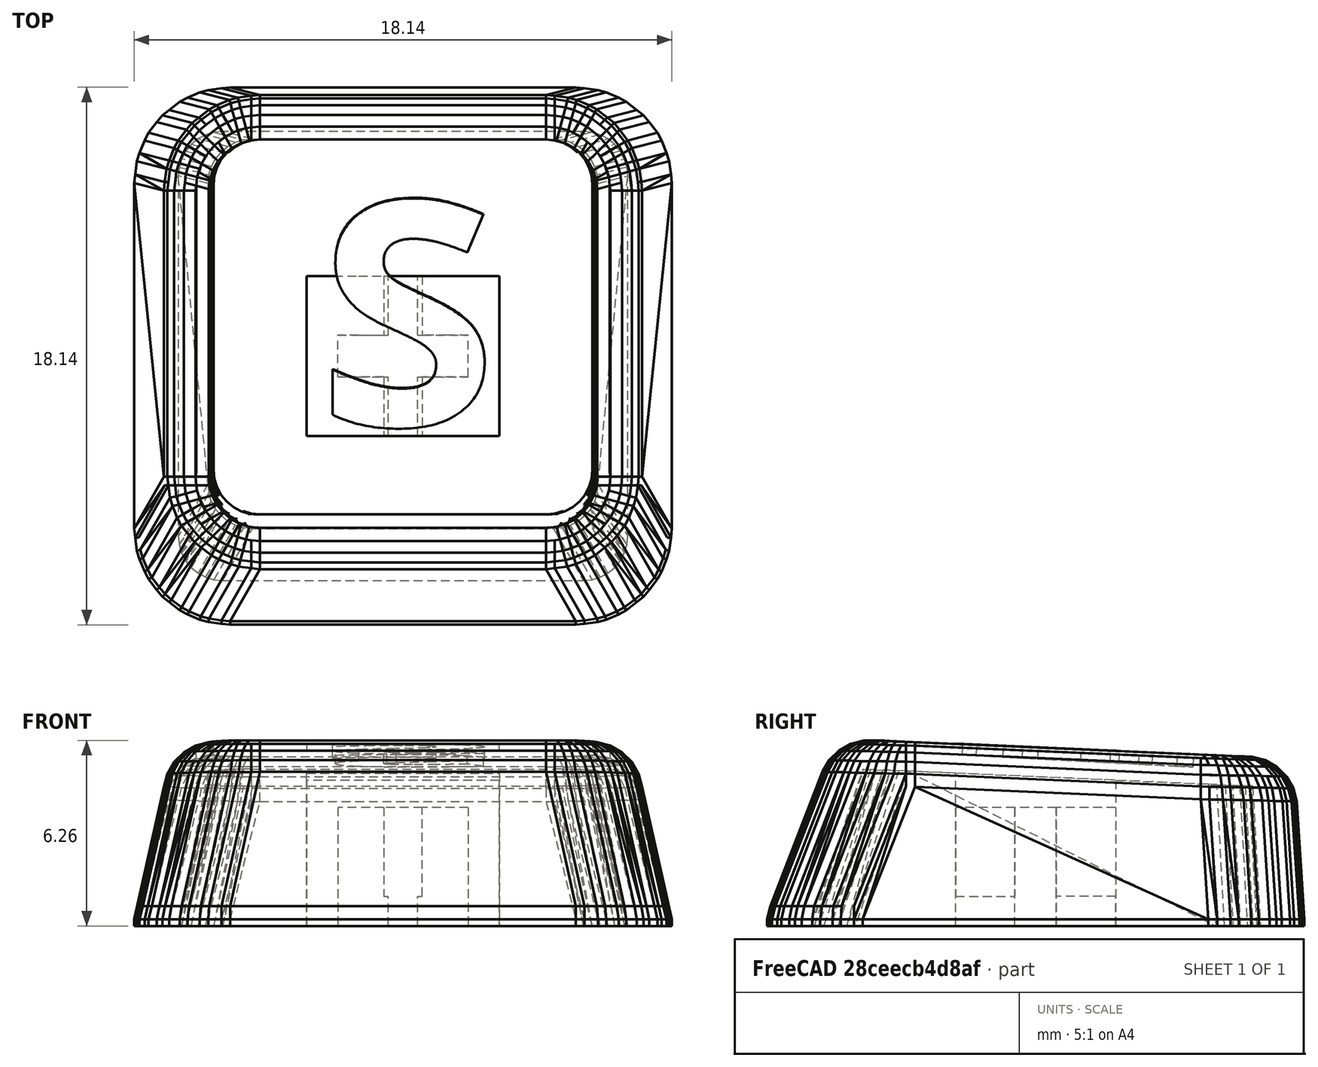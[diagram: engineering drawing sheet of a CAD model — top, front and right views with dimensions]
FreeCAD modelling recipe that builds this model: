
FCSTD DOCUMENT  (FreeCAD 0.18R16131 (Git))
Label: input
License: All rights reserved
LicenseURL: http://en.wikipedia.org/wiki/All_rights_reserved
objects: Part::Box×4, Part::Feature×1, Part::MultiFuse×1, Part::Part2DObjectPython×1, Part::Extrusion×1, Part::Cut×1
note: 9 computed .brp shape members not serialized (recipe doc carries the construction recipe); baked Part::Feature solids carry a one-line shape summary decoded from their .brp

FEATURE [Part::Feature] Solid
  shape: bbox 18.13 x 18.13 x 6.262 mm, 1259 faces (baked)
FEATURE [Part::Box] Box  label="Cube"
  AttacherType = Attacher::AttachEngine3D
  Height = 1
  Length = 1
  Placement = pos=(0.5,-2.7,0) rot=(0,0,1;0rad)
  Width = 2
FEATURE [Part::Box] Box001  label="Cube001"
  AttacherType = Attacher::AttachEngine3D
  Height = 1
  Length = 1
  Placement = pos=(-1.5,0.7,0) rot=(0,0,1;0rad)
  Width = 2
FEATURE [Part::Box] Box002  label="Cube002"
  AttacherType = Attacher::AttachEngine3D
  Height = 1
  Length = 1
  Placement = pos=(-1.5,-2.7,0) rot=(0,0,1;0rad)
  Width = 2
FEATURE [Part::Box] Box003  label="Cube003"
  AttacherType = Attacher::AttachEngine3D
  Height = 1
  Length = 1
  Placement = pos=(0.5,0.7,0) rot=(0,0,1;0rad)
  Width = 2
FEATURE [Part::MultiFuse] Fusion
  Shapes = -> [Solid,Box002,Box001,Box,Box003]
FEATURE [Part::Part2DObjectPython] ShapeString  # Draft 2D object (typed FeaturePython)
  FontFile = <userpath>/A6E4-ED97/3dprinting/fonts/open-sans/OpenSans-Bold.ttf
  Placement = pos=(-36.88,31.64,36.88) rot=(0,1,0;0rad)
  Size = 10
  String = S
  Tracking = 0
FEATURE [Part::Extrusion] Extrude
  Base = -> ShapeString
  Dir = (0,0,1)
  DirMode = 2
  FaceMakerClass = Part::FaceMakerBullseye
  LengthFwd = 0.5
  LengthRev = 0
  Placement = pos=(34,-36,-29.4) rot=(1,0,0;-0.05236rad)
  Solid = false
  Symmetric = false
FEATURE [Part::Cut] Cut
  Base = -> Fusion
  Tool = -> Extrude
